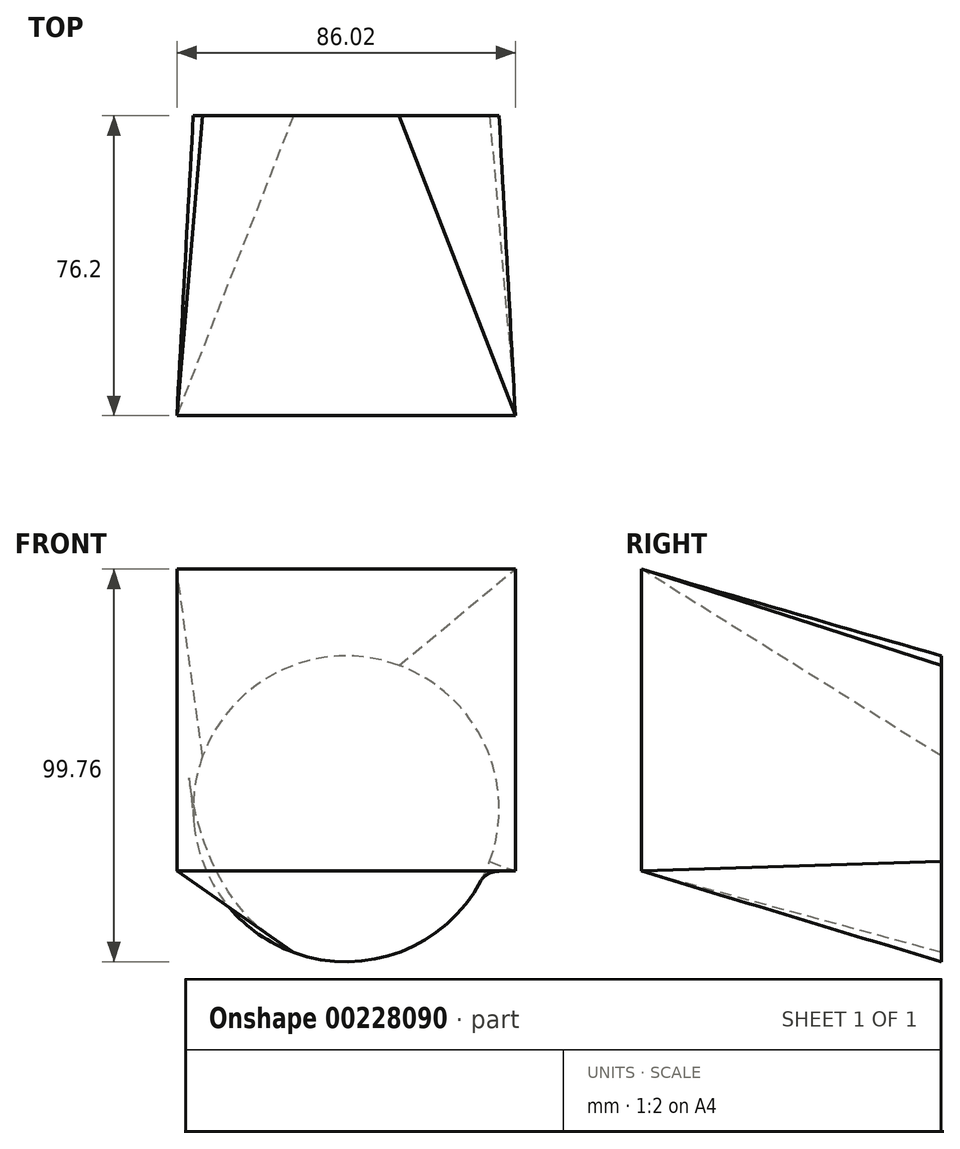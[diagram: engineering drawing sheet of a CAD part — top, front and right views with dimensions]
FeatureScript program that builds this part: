
annotation { "Feature Type Name" : "Feature", "Feature Type Description" : "" }
export const myFeature = defineFeature(function(context is Context, id is Id, definition is map)
    precondition{}
    {
        {
            var Q0;
            Q0=qCreatedBy(makeId("Front.planeOp"),FACE);
            var sketch = newSketch(context, id + "F0", { "sketchPlane" : qUnion([Q0])});
            skCircle(sketch, "E0", {"center": v(0, 0) * mm, "radius": 38.85 * mm});
            skSolve(sketch);
        }
        {
            var Q0;
            Q0=qCreatedBy(makeId("Front.planeOp"),FACE);
            cPlane(context, id + "F1", {"entities" : qUnion([Q0]), "cplaneType" : CPlaneType.OFFSET, "offset" : 76.2 * mm, "width" : 152.4 * mm, "height" : 152.4 * mm});
        }
        {
            var Q0;
            Q0=qCreatedBy(id+"F1.planeOp",FACE);
            var sketch = newSketch(context, id + "F2", { "sketchPlane" : qUnion([Q0])});
            skLineSegment(sketch, "E1.bottom", {"start": v(43.01, -15.81) * mm, "end": v(-43.01, -15.81) * mm});
            skLineSegment(sketch, "E1.top", {"start": v(43.01, 60.91) * mm, "end": v(-43.01, 60.91) * mm});
            skLineSegment(sketch, "E1.left", {"start": v(43.01, -15.81) * mm, "end": v(43.01, 60.91) * mm});
            skLineSegment(sketch, "E1.right", {"start": v(-43.01, -15.81) * mm, "end": v(-43.01, 60.91) * mm});
            skPoint(sketch, "E1.middle", {"position": v(0, 22.55) * mm});
            skSolve(sketch);
        }
        {
            var Q0;
            Q0=makeQuery(id+"F0.imprint","IMPRINT",FACE,{"disambiguationData":[TD([[makeQuery(id+"F0.imprint","IMPRINT",EDGE,{"derivedFrom":sQuery(id+"F0.wireOp",EDGE,"E0")}),1.0]])]});
            var Q1;
            Q1=makeQuery(id+"F2.imprint","IMPRINT",FACE,{"disambiguationData":[TD([[makeQuery(id+"F2.imprint","IMPRINT",EDGE,{"derivedFrom":sQuery(id+"F2.wireOp",EDGE,"E1.bottom")}),-1.0]])]});
            loft(context, id + "F3", {"sheetProfilesArray" : [{ "sheetProfileEntities" : qUnion([Q0]) }, { "sheetProfileEntities" : qUnion([Q1]) }]});
        }
    });
